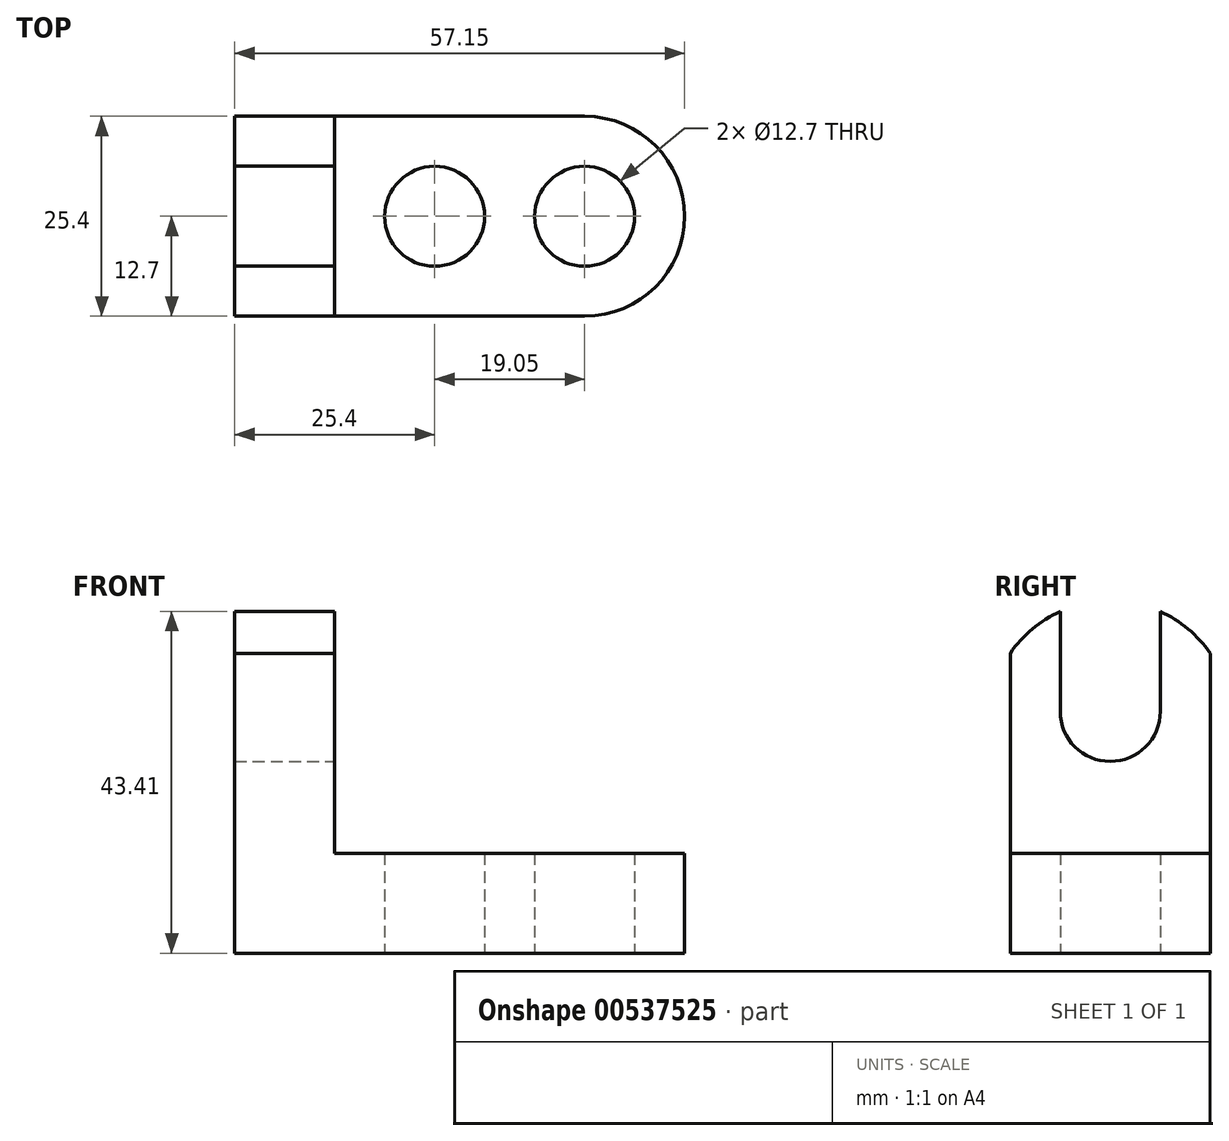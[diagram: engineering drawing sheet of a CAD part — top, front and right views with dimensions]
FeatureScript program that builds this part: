
annotation { "Feature Type Name" : "Feature", "Feature Type Description" : "" }
export const myFeature = defineFeature(function(context is Context, id is Id, definition is map)
    precondition{}
    {
        {
            var Q0;
            Q0=qCreatedBy(makeId("Top.planeOp"),FACE);
            var sketch = newSketch(context, id + "F0", { "sketchPlane" : qUnion([Q0])});
            skLineSegment(sketch, "E0", {"start": v(0, 0) * mm, "end": v(44.45, 0) * mm});
            skLineSegment(sketch, "E1", {"start": v(0, 0) * mm, "end": v(0, 25.4) * mm});
            skLineSegment(sketch, "E2", {"start": v(0, 25.4) * mm, "end": v(44.45, 25.4) * mm});
            skArc(sketch, "E3", {"start": v(44.45, 0) * mm, "mid": v(57.15, 12.7) * mm, "end": v(44.45, 25.4) * mm});
            skCircle(sketch, "E4", {"center": v(44.45, 12.7) * mm, "radius": 6.35 * mm});
            skCircle(sketch, "E5", {"center": v(25.4, 12.7) * mm, "radius": 6.35 * mm});
            skSolve(sketch);
        }
        {
            var Q0;
            Q0 = qSketchRegion(id + "F0", true);
            extrude(context, id + "F1", {"entities" : qUnion([Q0]), "depth" : 12.7 * mm, "offsetDistance" : 25.4 * mm});
        }
        {
            var Q0;
            Q0=makeQuery(id+"F1.opExtrude","SWEPT_FACE",FACE,{"disambiguationData":[OSD([sQuery(id+"F0.wireOp",EDGE,"E0")])]});
            var sketch = newSketch(context, id + "F2", { "sketchPlane" : qUnion([Q0])});
            skLineSegment(sketch, "E6", {"start": v(0, 12.7) * mm, "end": v(0, 38.1) * mm});
            skLineSegment(sketch, "E7", {"start": v(0, 38.1) * mm, "end": v(12.7, 38.1) * mm});
            skLineSegment(sketch, "E8", {"start": v(12.7, 38.1) * mm, "end": v(12.7, 12.7) * mm});
            skSolve(sketch);
        }
        {
            var Q0;
            Q0 = qSketchRegion(id + "F2", true);
            var Q1;
            {var subQ0=sQuery(id+"F2.wireOp",EDGE,"E6");Q1=makeQuery(id+"F2.imprint","IMPRINT",FACE,{"disambiguationData":[TD([[makeQuery(id+"F2.imprint","IMPRINT",EDGE,{"derivedFrom":subQ0}),-1.0]])]});}
            extrude(context, id + "F3", {"entities" : qUnion([Q0, Q1]), "operationType" : NewBodyOperationType.ADD, "oppositeDirection" : true, "depth" : 25.4 * mm, "offsetDistance" : 25.4 * mm});
        }
        {
            var Q0;
            Q0=makeQuery(id+"F3.opExtrude","SWEPT_FACE",FACE,{"disambiguationData":[OSD([sQuery(id+"F2.wireOp",EDGE,"E8")])]});
            var sketch = newSketch(context, id + "F4", { "sketchPlane" : qUnion([Q0])});
            skLineSegment(sketch, "E9", {"start": v(0, 38.1) * mm, "end": v(0, 44.45) * mm});
            skLineSegment(sketch, "E10", {"start": v(0, 44.45) * mm, "end": v(25.4, 44.45) * mm});
            skLineSegment(sketch, "E11", {"start": v(25.4, 44.45) * mm, "end": v(25.4, 38.1) * mm});
            skSolve(sketch);
        }
        {
            var Q0;
            Q0 = qSketchRegion(id + "F4", true);
            var Q1;
            Q1=makeQuery(id+"F4.imprint","IMPRINT",FACE,{"disambiguationData":[TD([[makeQuery(id+"F4.imprint","IMPRINT",EDGE,{"derivedFrom":sQuery(id+"F4.wireOp",EDGE,"E9")}),-1.0]])]});
            extrude(context, id + "F5", {"entities" : qUnion([Q0, Q1]), "operationType" : NewBodyOperationType.ADD, "oppositeDirection" : true, "depth" : 12.7 * mm, "offsetDistance" : 25.4 * mm});
        }
        {
            var Q0;
            {var subQ0=sQuery(id+"F2.wireOp",EDGE,"E8");Q0=makeQuery(id+"F5.boolean.opBoolean","MERGE",FACE,{"derivedFrom":[makeQuery(id+"F3.opExtrude","SWEPT_FACE",FACE,{"disambiguationData":[OSD([subQ0])]}),makeQuery(id+"F5.opExtrude","CAP_FACE",FACE,{"disambiguationData":[OSD([sQuery(id+"F2.wireOp",EDGE,"E7"),subQ0,sQuery(id+"F4.wireOp",EDGE,"E9"),sQuery(id+"F4.wireOp",EDGE,"E10"),sQuery(id+"F4.wireOp",EDGE,"E11")])],"isStart":true})]});}
            var sketch = newSketch(context, id + "F6", { "sketchPlane" : qUnion([Q0])});
            skArc(sketch, "E12", {"start": v(25.4, 38.1) * mm, "mid": v(12.7, 44.78) * mm, "end": v(0, 38.1) * mm});
            skSolve(sketch);
        }
        {
            var Q0;
            {var subQ0=sQuery(id+"F6.wireOp",EDGE,"E12");var subQ3=makeQuery(id+"F5.opExtrude","CAP_EDGE",EDGE,{"disambiguationData":[OSD([sQuery(id+"F4.wireOp",EDGE,"E10")])],"isStart":true});var subQ4=makeQuery(id+"F6.imprint","INTERSECT",VERTEX,{"disambiguationData":[OD(0.0)],"derivedFrom":[subQ3,subQ0]});Q0=makeQuery(id+"F6.imprint","IMPRINT",FACE,{"disambiguationData":[TD([[makeQuery(id+"F6.imprint","IMPRINT",EDGE,{"disambiguationData":[TD([[subQ4,1.0]])],"derivedFrom":subQ0}),-1.0]])]});}
            var Q1;
            {var subQ0=sQuery(id+"F6.wireOp",EDGE,"E12");var subQ3=makeQuery(id+"F5.opExtrude","CAP_EDGE",EDGE,{"disambiguationData":[OSD([sQuery(id+"F4.wireOp",EDGE,"E10")])],"isStart":true});var subQ4=makeQuery(id+"F6.imprint","INTERSECT",VERTEX,{"disambiguationData":[OD(1.0)],"derivedFrom":[subQ3,subQ0]});Q1=makeQuery(id+"F6.imprint","IMPRINT",FACE,{"disambiguationData":[TD([[makeQuery(id+"F6.imprint","IMPRINT",EDGE,{"disambiguationData":[TD([[subQ4,-1.0]])],"derivedFrom":subQ0}),-1.0]])]});}
            extrude(context, id + "F7", {"entities" : qUnion([Q0, Q1]), "operationType" : NewBodyOperationType.REMOVE, "oppositeDirection" : true, "depth" : 25.4 * mm, "offsetDistance" : 25.4 * mm});
        }
        {
            var Q0;
            {var subQ0=sQuery(id+"F2.wireOp",EDGE,"E8");Q0=makeQuery(id+"F5.boolean.opBoolean","MERGE",FACE,{"derivedFrom":[makeQuery(id+"F3.opExtrude","SWEPT_FACE",FACE,{"disambiguationData":[OSD([subQ0])]}),makeQuery(id+"F5.opExtrude","CAP_FACE",FACE,{"disambiguationData":[OSD([sQuery(id+"F2.wireOp",EDGE,"E7"),subQ0,sQuery(id+"F4.wireOp",EDGE,"E9"),sQuery(id+"F4.wireOp",EDGE,"E10"),sQuery(id+"F4.wireOp",EDGE,"E11")])],"isStart":true})]});}
            var sketch = newSketch(context, id + "F8", { "sketchPlane" : qUnion([Q0])});
            skLineSegment(sketch, "E13", {"start": v(6.35, 43.4) * mm, "end": v(6.35, 30.7) * mm});
            skLineSegment(sketch, "E14", {"start": v(19.05, 43.4) * mm, "end": v(19.05, 30.7) * mm});
            skArc(sketch, "E15", {"start": v(6.35, 30.7) * mm, "mid": v(12.7, 24.36) * mm, "end": v(19.05, 30.7) * mm});
            skSolve(sketch);
        }
        {
            var Q0;
            Q0 = qSketchRegion(id + "F8", true);
            var Q1;
            {var subQ3=sQuery(id+"F8.wireOp",EDGE,"E13");Q1=makeQuery(id+"F8.imprint","IMPRINT",FACE,{"disambiguationData":[TD([[makeQuery(id+"F8.imprint","IMPRINT",EDGE,{"derivedFrom":subQ3}),1.0]])]});}
            extrude(context, id + "F9", {"entities" : qUnion([Q0, Q1]), "operationType" : NewBodyOperationType.REMOVE, "oppositeDirection" : true, "depth" : 25.4 * mm, "offsetDistance" : 25.4 * mm});
        }
    });
